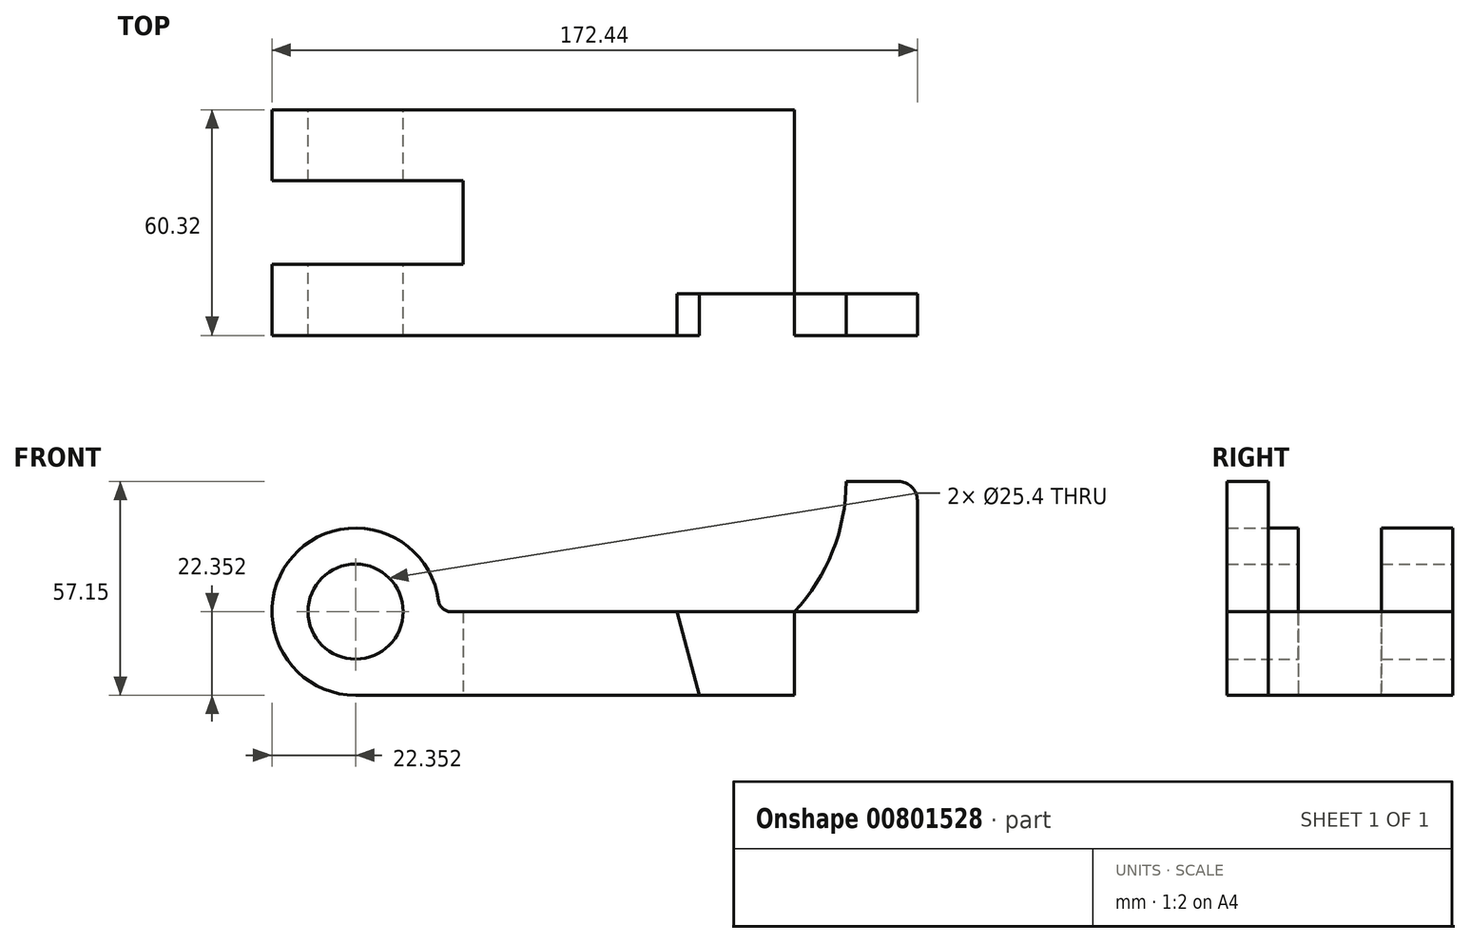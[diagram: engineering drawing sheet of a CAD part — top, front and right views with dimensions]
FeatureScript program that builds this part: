
annotation { "Feature Type Name" : "Feature", "Feature Type Description" : "" }
export const myFeature = defineFeature(function(context is Context, id is Id, definition is map)
    precondition{}
    {
        {
            var Q0;
            Q0=qCreatedBy(makeId("Front.planeOp"),FACE);
            var sketch = newSketch(context, id + "F0", { "sketchPlane" : qUnion([Q0])});
            skLineSegment(sketch, "E0.bottom", {"start": v(0, 0) * mm, "end": v(-194.2, 0) * mm});
            skLineSegment(sketch, "E0.top", {"start": v(-49.2, 57.15) * mm, "end": v(-63.17, 57.15) * mm});
            skLineSegment(sketch, "E0.left", {"start": v(0, 0) * mm, "end": v(0, 22.35) * mm});
            skLineSegment(sketch, "E1.bottom", {"start": v(-194.2, 0) * mm, "end": v(0, 0) * mm});
            skLineSegment(sketch, "E1.top", {"start": v(-216.56, 22.35) * mm, "end": v(-7.87, 22.35) * mm});
            skLineSegment(sketch, "E1.right", {"start": v(0, 0) * mm, "end": v(0, 14.48) * mm});
            skLineSegment(sketch, "E2", {"start": v(-76.96, 22.35) * mm, "end": v(-76.96, 0) * mm});
            skLineSegment(sketch, "E3", {"start": v(-194.2, 71.24) * mm, "end": v(-194.2, -42.33) * mm, "construction": true});
            skCircle(sketch, "E4", {"center": v(-194.2, 22.35) * mm, "radius": 12.7 * mm});
            skCircle(sketch, "E5", {"center": v(-194.2, 22.35) * mm, "radius": 22.35 * mm});
            skLineSegment(sketch, "E6", {"start": v(-102.36, 0) * mm, "end": v(-108.36, 22.35) * mm});
            skLineSegment(sketch, "E7", {"start": v(-44.12, 22.35) * mm, "end": v(-44.12, 52.07) * mm});
            skLineSegment(sketch, "E8", {"start": v(-63.17, 74.18) * mm, "end": v(-63.17, 57.15) * mm, "construction": true});
            skArc(sketch, "E9", {"start": v(-63.17, 57.15) * mm, "mid": v(-66.74, 38.44) * mm, "end": v(-76.96, 22.35) * mm});
            skPoint(sketch, "E10.visualSharp", {"position": v(0, 22.35) * mm});
            skArc(sketch, "E10.filletArc", {"start": v(0, 14.48) * mm, "mid": v(-2.3, 20.05) * mm, "end": v(-7.87, 22.35) * mm});
            skPoint(sketch, "E11.visualSharp", {"position": v(-44.12, 57.15) * mm});
            skArc(sketch, "E11.filletArc", {"start": v(-44.12, 52.07) * mm, "mid": v(-45.6, 55.66) * mm, "end": v(-49.2, 57.15) * mm});
            skLineSegment(sketch, "E12", {"start": v(-165.93, 22.35) * mm, "end": v(-165.93, 0) * mm});
            skSolve(sketch);
        }
        {
            var Q0;
            {var subQ0=sQuery(id+"F0.wireOp",EDGE,"E5");var subQ1=sQuery(id+"F0.wireOp",EDGE,"E1.top");var subQ2=makeQuery(id+"F0.imprint","INTERSECT",VERTEX,{"disambiguationData":[OD(0.0)],"derivedFrom":[subQ1,subQ0]});Q0=makeQuery(id+"F0.imprint","IMPRINT",FACE,{"disambiguationData":[TD([[makeQuery(id+"F0.imprint","IMPRINT",EDGE,{"disambiguationData":[TD([[subQ2,-1.0]])],"derivedFrom":subQ1}),1.0]])]});}
            var Q1;
            {var subQ0=sQuery(id+"F0.wireOp",EDGE,"E5");var subQ2=sQuery(id+"F0.wireOp",EDGE,"E1.top");var subQ3=makeQuery(id+"F0.imprint","INTERSECT",VERTEX,{"disambiguationData":[OD(0.0)],"derivedFrom":[subQ2,subQ0]});Q1=makeQuery(id+"F0.imprint","IMPRINT",FACE,{"disambiguationData":[TD([[makeQuery(id+"F0.imprint","IMPRINT",EDGE,{"disambiguationData":[TD([[subQ3,-1.0]])],"derivedFrom":subQ2}),-1.0]])]});}
            var Q2;
            {var subQ3=sQuery(id+"F0.wireOp",EDGE,"E6");Q2=makeQuery(id+"F0.imprint","IMPRINT",FACE,{"disambiguationData":[TD([[makeQuery(id+"F0.imprint","IMPRINT",EDGE,{"derivedFrom":subQ3}),1.0]])]});}
            var Q3;
            {var subQ0=sQuery(id+"F0.wireOp",EDGE,"E1.right");Q3=makeQuery(id+"F0.imprint","IMPRINT",FACE,{"disambiguationData":[TD([[makeQuery(id+"F0.imprint","IMPRINT",EDGE,{"derivedFrom":subQ0}),1.0]])]});}
            var Q4;
            {var subQ0=sQuery(id+"F0.wireOp",EDGE,"E2");Q4=makeQuery(id+"F0.imprint","IMPRINT",FACE,{"disambiguationData":[TD([[makeQuery(id+"F0.imprint","IMPRINT",EDGE,{"derivedFrom":subQ0}),-1.0]])]});}
            var Q5;
            {var subQ3=sQuery(id+"F0.wireOp",EDGE,"E12");Q5=makeQuery(id+"F0.imprint","IMPRINT",FACE,{"disambiguationData":[TD([[makeQuery(id+"F0.imprint","IMPRINT",EDGE,{"derivedFrom":subQ3}),-1.0]])]});}
            extrude(context, id + "F1", {"entities" : qUnion([Q0, Q1, Q2, Q3, Q4, Q5]), "depth" : 60.32 * mm, "offsetDistance" : 25.4 * mm, "symmetric" : true});
        }
        {
            var Q0;
            Q0=makeQuery(id+"F0.imprint","IMPRINT",FACE,{"disambiguationData":[TD([[makeQuery(id+"F0.imprint","IMPRINT",EDGE,{"derivedFrom":sQuery(id+"F0.wireOp",EDGE,"E0.top")}),1.0]])]});
            var Q1;
            Q1=makeQuery(id+"F1.opExtrude","CAP_FACE",FACE,{"disambiguationData":[OSD([sQuery(id+"F0.wireOp",EDGE,"E1.bottom"),sQuery(id+"F0.wireOp",EDGE,"E1.top"),sQuery(id+"F0.wireOp",EDGE,"E1.right"),sQuery(id+"F0.wireOp",EDGE,"E4"),sQuery(id+"F0.wireOp",EDGE,"E5"),sQuery(id+"F0.wireOp",EDGE,"E10.filletArc")])],"isStart":false});
            extrude(context, id + "F2", {"entities" : qUnion([Q0]), "operationType" : NewBodyOperationType.ADD, "endBound" : BoundingType.UP_TO_SURFACE, "depth" : 25.4 * mm, "endBoundEntityFace" : qUnion([Q1]), "offsetDistance" : 25.4 * mm, "offsetOppositeDirection" : true, "hasSecondDirection" : true, "secondDirectionOppositeDirection" : false, "secondDirectionDepth" : 19.05 * mm});
        }
        {
            var Q0;
            {var subQ0=sQuery(id+"F0.wireOp",EDGE,"E2");Q0=makeQuery(id+"F0.imprint","IMPRINT",FACE,{"disambiguationData":[TD([[makeQuery(id+"F0.imprint","IMPRINT",EDGE,{"derivedFrom":subQ0}),-1.0]])]});}
            extrude(context, id + "F3", {"entities" : qUnion([Q0]), "operationType" : NewBodyOperationType.REMOVE, "endBound" : BoundingType.UP_TO_NEXT, "depth" : 25.4 * mm, "offsetDistance" : 25.4 * mm, "hasSecondDirection" : true, "secondDirectionOppositeDirection" : false, "secondDirectionDepth" : 19.05 * mm});
        }
        {
            var Q0;
            Q0=makeQuery(id+"F1.opExtrude","SWEPT_EDGE",EDGE,{"disambiguationData":[OSD([sQuery(id+"F0.wireOp",EDGE,"E1.top"),sQuery(id+"F0.wireOp",EDGE,"E5")])]});
            fillet(context, id + "F4", {"entities" : qUnion([Q0]), "radius" : 3.3 * mm, "tangentPropagation" : true, "allowEdgeOverflow" : false});
        }
        {
            var Q0;
            Q0=qCreatedBy(makeId("Top.planeOp"),FACE);
            var sketch = newSketch(context, id + "F5", { "sketchPlane" : qUnion([Q0])});
            skLineSegment(sketch, "E13", {"start": v(-165.45, 0) * mm, "end": v(-165.45, -11.16) * mm});
            skLineSegment(sketch, "E14", {"start": v(-165.45, -11.16) * mm, "end": v(-218.3, -11.16) * mm});
            skLineSegment(sketch, "E15", {"start": v(-218.3, -11.16) * mm, "end": v(-218.3, 11.16) * mm});
            skLineSegment(sketch, "E16", {"start": v(-218.3, 11.16) * mm, "end": v(-165.45, 11.16) * mm});
            skLineSegment(sketch, "E17", {"start": v(-165.45, 11.16) * mm, "end": v(-165.45, 0) * mm});
            skSolve(sketch);
        }
        {
            var Q0;
            Q0=qSketchRegion(id+"F5",true);
            extrude(context, id + "F6", {"entities" : qUnion([Q0]), "operationType" : NewBodyOperationType.REMOVE, "endBound" : BoundingType.THROUGH_ALL, "depth" : 25.4 * mm, "offsetDistance" : 25.4 * mm});
        }
        {
            var Q0;
            Q0=makeQuery(id+"F1.opExtrude","SWEPT_FACE",FACE,{"disambiguationData":[OSD([sQuery(id+"F0.wireOp",EDGE,"E1.top")])]});
            var sketch = newSketch(context, id + "F7", { "sketchPlane" : qUnion([Q0])});
            skCircle(sketch, "E18", {"center": v(-38.86, 7.81) * mm, "radius": 6.35 * mm});
            skSolve(sketch);
        }
        {
            var Q0;
            Q0=qSketchRegion(id+"F7",true);
            extrude(context, id + "F8", {"entities" : qUnion([Q0]), "operationType" : NewBodyOperationType.REMOVE, "endBound" : BoundingType.THROUGH_ALL, "oppositeDirection" : true, "depth" : 25.4 * mm, "offsetDistance" : 25.4 * mm});
        }
    });
